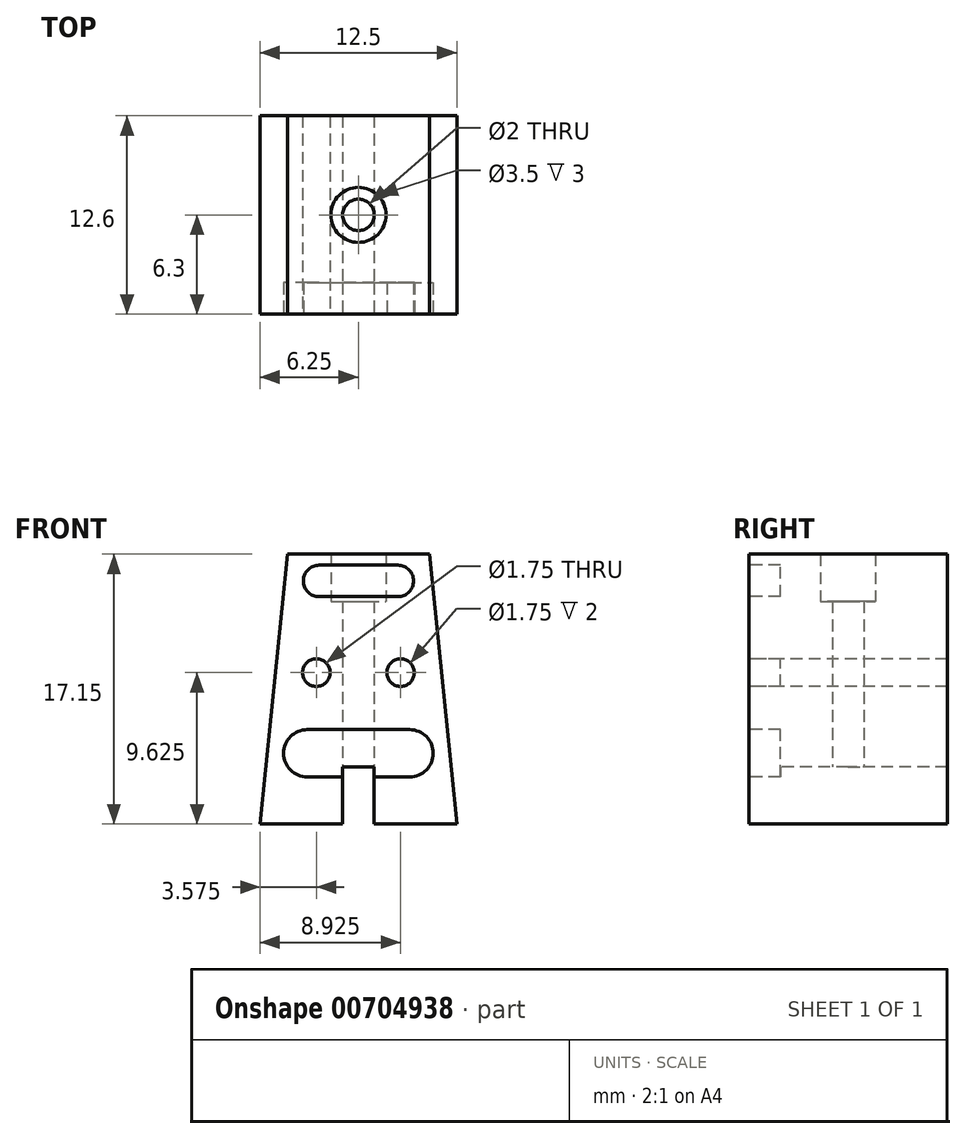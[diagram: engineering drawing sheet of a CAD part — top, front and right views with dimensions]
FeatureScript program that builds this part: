
annotation { "Feature Type Name" : "Feature", "Feature Type Description" : "" }
export const myFeature = defineFeature(function(context is Context, id is Id, definition is map)
    precondition{}
    {
        {
            var Q0;
            Q0=qCreatedBy(makeId("Front.planeOp"),FACE);
            var sketch = newSketch(context, id + "F0", { "sketchPlane" : qUnion([Q0])});
            skLineSegment(sketch, "E0", {"start": v(6.25, 0) * mm, "end": v(4.5, 17.15) * mm});
            skLineSegment(sketch, "E1", {"start": v(0, 3.65) * mm, "end": v(1, 3.65) * mm});
            skLineSegment(sketch, "E2", {"start": v(1, 3.65) * mm, "end": v(1, 0) * mm});
            skLineSegment(sketch, "E3", {"start": v(1, 0) * mm, "end": v(6.25, 0) * mm});
            skLineSegment(sketch, "E4", {"start": v(4.5, 17.15) * mm, "end": v(0, 17.15) * mm});
            skLineSegment(sketch, "E5.MirrorCS", {"start": v(-6.25, 0) * mm, "end": v(-4.5, 17.15) * mm});
            skLineSegment(sketch, "E6.MirrorCS", {"start": v(0, 3.65) * mm, "end": v(-1, 3.65) * mm});
            skLineSegment(sketch, "E7.MirrorCS", {"start": v(-1, 3.65) * mm, "end": v(-1, 0) * mm});
            skLineSegment(sketch, "E8.MirrorCS", {"start": v(-1, 0) * mm, "end": v(-6.25, 0) * mm});
            skLineSegment(sketch, "E9.MirrorCS", {"start": v(-4.5, 17.15) * mm, "end": v(0, 17.15) * mm});
            skLineSegment(sketch, "E10", {"start": v(0, 6) * mm, "end": v(-3.25, 6) * mm});
            skLineSegment(sketch, "E11", {"start": v(-3.25, 3) * mm, "end": v(-1, 3) * mm});
            skArc(sketch, "E12", {"start": v(-3.25, 6) * mm, "mid": v(-4.75, 4.5) * mm, "end": v(-3.25, 3) * mm});
            skLineSegment(sketch, "E13.MirrorCS", {"start": v(0, 6) * mm, "end": v(3.25, 6) * mm});
            skLineSegment(sketch, "E14.MirrorCS", {"start": v(3.25, 3) * mm, "end": v(1, 3) * mm});
            skArc(sketch, "E15.MirrorCS", {"start": v(3.25, 6) * mm, "mid": v(4.75, 4.5) * mm, "end": v(3.25, 3) * mm});
            skPoint(sketch, "E16", {"position": v(-4.75, 4.5) * mm});
            skLineSegment(sketch, "E17", {"start": v(1, 3) * mm, "end": v(-1, 3) * mm});
            skPoint(sketch, "E18", {"position": v(2.67, 9.62) * mm});
            skLineSegment(sketch, "E19.MirrorCS", {"start": v(0, 16.45) * mm, "end": v(2.5, 16.45) * mm});
            skLineSegment(sketch, "E20.MirrorCS", {"start": v(0, 14.45) * mm, "end": v(2.5, 14.45) * mm});
            skArc(sketch, "E21.MirrorCS", {"start": v(2.5, 16.45) * mm, "mid": v(3.5, 15.45) * mm, "end": v(2.5, 14.45) * mm});
            skCircle(sketch, "E22", {"center": v(2.67, 9.62) * mm, "radius": 0.88 * mm});
            skLineSegment(sketch, "E23", {"start": v(0, 7.27) * mm, "end": v(0, 11.23) * mm, "construction": true});
            skCircle(sketch, "E24.MirrorC", {"center": v(-2.68, 9.62) * mm, "radius": 0.88 * mm});
            skLineSegment(sketch, "E25.MirrorCS", {"start": v(0, 14.45) * mm, "end": v(-2.5, 14.45) * mm});
            skLineSegment(sketch, "E26.MirrorCS", {"start": v(0, 16.45) * mm, "end": v(-2.5, 16.45) * mm});
            skArc(sketch, "E27.MirrorCS", {"start": v(-2.5, 16.45) * mm, "mid": v(-3.5, 15.45) * mm, "end": v(-2.5, 14.45) * mm});
            skSolve(sketch);
        }
        {
            var Q0;
            Q0=makeQuery(id+"F0.imprint","IMPRINT",FACE,{"disambiguationData":[TD([[makeQuery(id+"F0.imprint","IMPRINT",EDGE,{"derivedFrom":sQuery(id+"F0.wireOp",EDGE,"E0")}),1.0]])]});
            var Q1;
            Q1=makeQuery(id+"F0.imprint","IMPRINT",FACE,{"disambiguationData":[TD([[makeQuery(id+"F0.imprint","IMPRINT",EDGE,{"derivedFrom":sQuery(id+"F0.wireOp",EDGE,"R2B9bVgT-NVim-9qVC-PTU1-5bjMkMqeAXZ5")}),1.0]])]});
            var Q2;
            Q2=makeQuery(id+"F0.imprint","IMPRINT",FACE,{"disambiguationData":[TD([[makeQuery(id+"F0.imprint","IMPRINT",EDGE,{"derivedFrom":sQuery(id+"F0.wireOp",EDGE,"E19.MirrorCS")}),-1.0]])]});
            var Q3;
            Q3=makeQuery(id+"F0.imprint","IMPRINT",FACE,{"disambiguationData":[TD([[makeQuery(id+"F0.imprint","IMPRINT",EDGE,{"derivedFrom":sQuery(id+"F0.wireOp",EDGE,"E24.MirrorC")}),-1.0]])]});
            var Q4;
            Q4=makeQuery(id+"F0.imprint","IMPRINT",FACE,{"disambiguationData":[TD([[makeQuery(id+"F0.imprint","IMPRINT",EDGE,{"derivedFrom":sQuery(id+"F0.wireOp",EDGE,"E22")}),1.0]])]});
            var Q5;
            {var subQ5=sQuery(id+"F0.wireOp",EDGE,"E1");Q5=makeQuery(id+"F0.imprint","IMPRINT",FACE,{"disambiguationData":[TD([[makeQuery(id+"F0.imprint","IMPRINT",EDGE,{"derivedFrom":subQ5}),1.0]])]});}
            extrude(context, id + "F1", {"entities" : qUnion([Q0, Q1, Q2, Q3, Q4, Q5]), "oppositeDirection" : true, "depth" : 12.6 * mm, "offsetDistance" : 25 * mm});
        }
        {
            var Q0;
            {var subQ5=sQuery(id+"F0.wireOp",EDGE,"E1");Q0=makeQuery(id+"F0.imprint","IMPRINT",FACE,{"disambiguationData":[TD([[makeQuery(id+"F0.imprint","IMPRINT",EDGE,{"derivedFrom":subQ5}),1.0]])]});}
            var Q1;
            Q1=makeQuery(id+"F0.imprint","IMPRINT",FACE,{"disambiguationData":[TD([[makeQuery(id+"F0.imprint","IMPRINT",EDGE,{"derivedFrom":sQuery(id+"F0.wireOp",EDGE,"E19.MirrorCS")}),-1.0]])]});
            var Q2;
            Q2=makeQuery(id+"F0.imprint","IMPRINT",FACE,{"disambiguationData":[TD([[makeQuery(id+"F0.imprint","IMPRINT",EDGE,{"derivedFrom":sQuery(id+"F0.wireOp",EDGE,"E22")}),1.0]])]});
            var Q3;
            Q3=makeQuery(id+"F0.imprint","IMPRINT",FACE,{"disambiguationData":[TD([[makeQuery(id+"F0.imprint","IMPRINT",EDGE,{"derivedFrom":sQuery(id+"F0.wireOp",EDGE,"E24.MirrorC")}),-1.0]])]});
            extrude(context, id + "F2", {"entities" : qUnion([Q0, Q1, Q2, Q3]), "operationType" : NewBodyOperationType.REMOVE, "oppositeDirection" : true, "depth" : 2 * mm, "offsetDistance" : 25 * mm});
        }
        {
            var Q0;
            Q0=makeQuery(id+"F1.opExtrude","SWEPT_FACE",FACE,{"disambiguationData":[OSD([sQuery(id+"F0.wireOp",EDGE,"E4"),sQuery(id+"F0.wireOp",EDGE,"E9.MirrorCS")])]});
            var sketch = newSketch(context, id + "F3", { "sketchPlane" : qUnion([Q0])});
            skLineSegment(sketch, "E28", {"start": v(0, 12.6) * mm, "end": v(0, 0) * mm, "construction": true});
            skPoint(sketch, "E29", {"position": v(0, 6.3) * mm});
            skSolve(sketch);
        }
        {
            var Q0;
            Q0=sQuery(id+"F3.wireOp",VERTEX,"E29");
            var Q1;
            Q1=makeQuery(id+"F1.opExtrude","SWEPT_BODY",BODY,{"disambiguationData":[OSD([sQuery(id+"F0.wireOp",EDGE,"E0"),sQuery(id+"F0.wireOp",EDGE,"E1"),sQuery(id+"F0.wireOp",EDGE,"E2"),sQuery(id+"F0.wireOp",EDGE,"E3"),sQuery(id+"F0.wireOp",EDGE,"E4"),sQuery(id+"F0.wireOp",EDGE,"E6.MirrorCS"),sQuery(id+"F0.wireOp",EDGE,"E7.MirrorCS"),sQuery(id+"F0.wireOp",EDGE,"E8.MirrorCS"),sQuery(id+"F0.wireOp",EDGE,"E5.MirrorCS"),sQuery(id+"F0.wireOp",EDGE,"E9.MirrorCS")])]});
            hole(context, id + "F4", {"style" : HoleStyle.C_BORE, "endStyle" : HoleEndStyle.BLIND, "holeDiameter" : 2 * mm, "cBoreDiameter" : 3.5 * mm, "cBoreDepth" : 3 * mm, "majorDiameter" : 5 * mm, "holeDepth" : 38 * mm, "isTappedThrough" : true, "tappedDepth" : 12 * mm, "tapClearance" : 3, "locations" : qUnion([Q0]), "scope" : qUnion([Q1]), "startStyle" : HoleStartStyle.PART});
        }
    });
